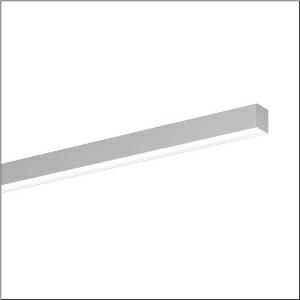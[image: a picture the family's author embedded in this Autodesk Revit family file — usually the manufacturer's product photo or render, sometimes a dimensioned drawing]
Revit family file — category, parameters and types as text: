
# Revit family: silica_21_51mx23da44sb
name_source: partatom
category: Lighting Fixtures
units: mm (PartAtom-declared; Revit-internal decimal feet)

## family parameters
Cut with Voids When Loaded = No
Host = Face
Light Source = No
Part Type = Normal
Room Calculation Point = No
Round Connector Dimension = Use Diameter
Shared = No

## types (1)
- --- (1 x LED, 3280 lm, 22.4 W, 4000K)
    Apparent Load = 22 VA
    CIE Flux Codes = 78 96 99 100 100
    Color Rendering = 80
    Color Temperature = 4000K
    Default Elevation = 1800 mm
    Description = Silica 21, office luminaire, primary optical cover: prismatic diffuser, of PMMA, CAT 2 (L<= 3000cd/m²), light emission: direct distribution, primary light characteristic: symmetric, installation type: surface-mounted, LED, rated luminous flux: 3.280lm, luminous efficacy: 146lm/W, light colour: 840, colour temperature: 4000K, control gear: DALI 2, with terminal, 3+2-pole, max. 2.5mm², mains connection: 220..240V, AC, 50/60Hz, rated input power: 22.4W, luminaire housing, of aluminium, metallic grey (RAL 9006), length: 1.204mm, width: 53mm, height: 53mm, protection rating (complete): IP20, insulation class (complete): insulation class I (protective earthing), certification: CE, permissible operating ambient temperature: 0..+35°C, standard: EN 50419, packaging unit: 1 piece
    Height = 53 mm
    Lamp = 1 x LED
    Lamp Light Flux = 3280 lm
    Lamp Power = 22.4 W
    Lamp count = 1
    Length = 1204 mm
    Luminous efficacy = 146 lm/W
    Manufacturer = Siteco
    ModVariant = No
    Model = 51MX23DA44SB
    Mounting Place = Ceiling
    Mounting Type = Surface mounted
    Number of Poles = 1
    OnlyDefault = Yes
    Power Factor = 1
    Product Name = Silica 21
    Product group = office luminaire | ceiling mounted
    ProductGroupID = 301
    Protection Class = Protection class I
    Protection Degree = IP 20
    RLX_Detail_Level = 1
    RLX_Emergency_Light_Flux = 0 lm
    RLX_Emergency_Type = 0
    RLX_Emergency_Type_DB = No
    RlxData = <blob elided: 21221 chars, md5=51aebc16>
    Socket = socket
    Standby Power = 0 W
    System Light Flux = 3280 lm
    System Power = 22 W
    Type Comments = factory setting: luminous flux: 100 % | dim-lin: 254 | 323 mA
    Type Image = l_1335933.jpg
    URL = http://relux.com
    VarID = @adj_028119
    Voltage = 0 V
    Weight = 0.00 kg
    Width = 53 mm

## geometry (parser evidence)
native form markers: Blend x4, Sweep x10
no freeform markers — native parametric forms only
